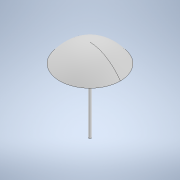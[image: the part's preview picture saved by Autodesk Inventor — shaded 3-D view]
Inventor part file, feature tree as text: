
AUTODESK INVENTOR PART (.ipt)
format: ipt  version: 2021 (Build 250183000, 183)  size: 216,576 bytes
history: native  units: in
note: dims shown in document units (in); Inventor stores cm internally (conversion verified against a paired STEP export)
features: sketch x3, extrude x2, revolve x1, shell x1
ambient origin geometry x8: Origin, YZ Plane, XZ Plane, XY Plane, X Axis, Y Axis, Z Axis, Center Point
bodies: Solid1 (feature_tree)
feature tree (7):
  revolve  "Revolution1"  [1 undecoded]
  shell  "Shell1"  Thickness=90.0deg
  extrude  "Extrusion2"  Depth=0.1181in
  extrude  "Extrusion1"  Depth=7.0in TaperAngle=0.0deg
  sketch  "Sketch1"  dims[d0=9.0in d1=5.25in d2=90.0deg]
  sketch  "Sketch2"  dims[d3=0.1181in d4=0.2362in]
  sketch  "Sketch3"  dims[d5=1.0in d6=0.0in d7=7.0in d8=0.0in]
note: 1 required parameter value undecoded (feature->parameter linkage not recoverable at this tier; creation-order binding heuristic only, values carry confidence <= 0.55)
